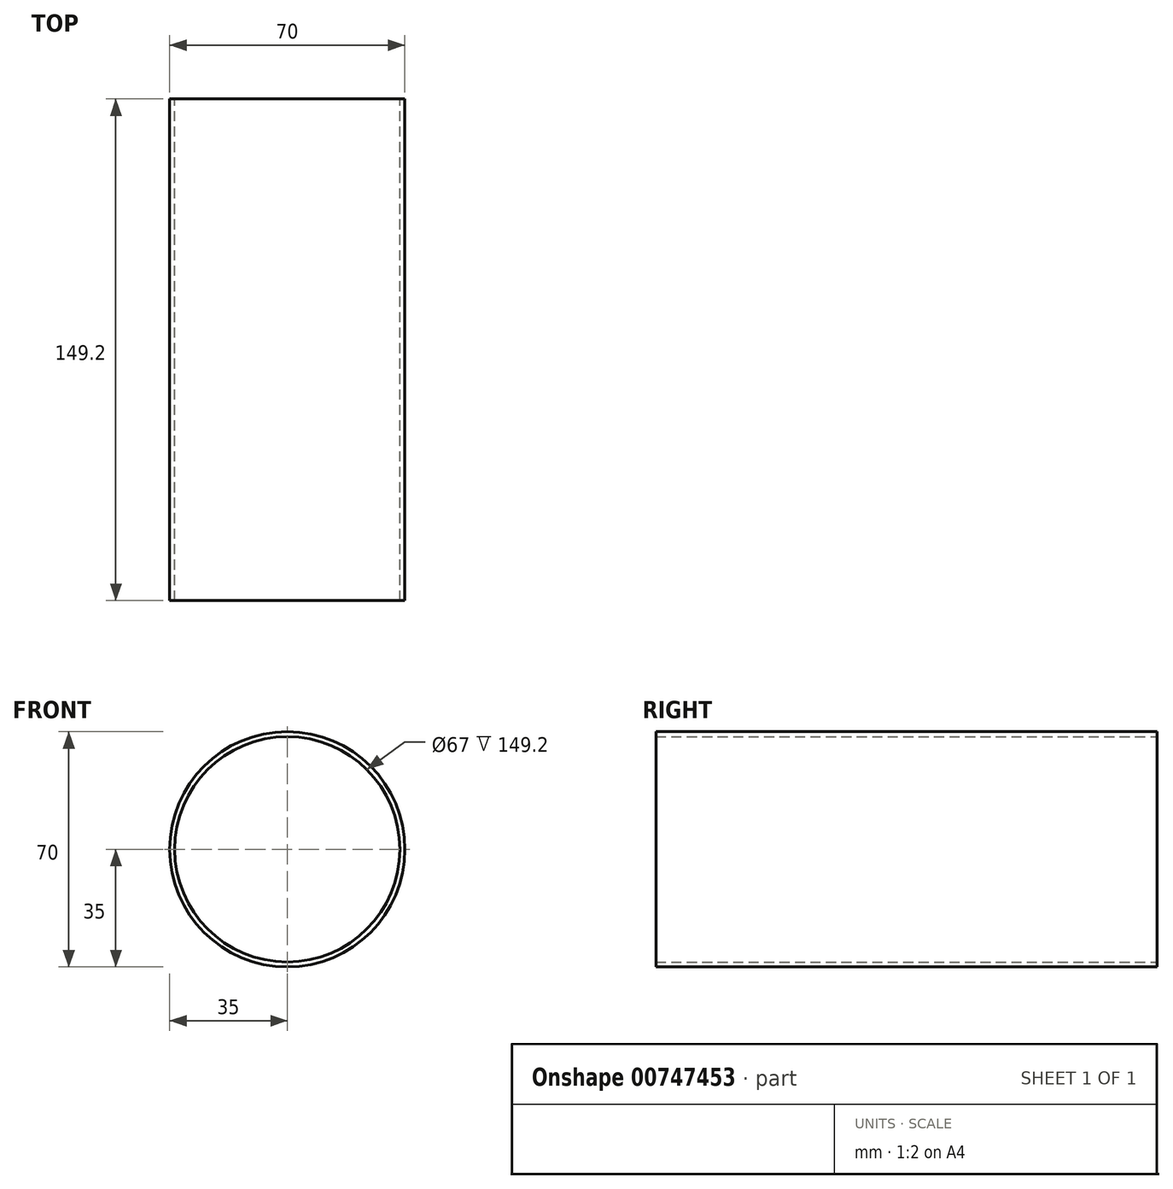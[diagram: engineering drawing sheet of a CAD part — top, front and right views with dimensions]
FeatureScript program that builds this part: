
annotation { "Feature Type Name" : "Feature", "Feature Type Description" : "" }
export const myFeature = defineFeature(function(context is Context, id is Id, definition is map)
    precondition{}
    {
        {
            var Q0;
            Q0=qCreatedBy(makeId("Front.planeOp"),FACE);
            var sketch = newSketch(context, id + "F0", { "sketchPlane" : qUnion([Q0])});
            skCircle(sketch, "E0", {"center": v(0, 0) * mm, "radius": 35 * mm});
            skCircle(sketch, "E1", {"center": v(0, 0) * mm, "radius": 33.5 * mm});
            skSolve(sketch);
        }
        {
            var Q0;
            Q0=makeQuery(id+"F0.imprint","IMPRINT",FACE,{"disambiguationData":[TD([[makeQuery(id+"F0.imprint","IMPRINT",EDGE,{"derivedFrom":sQuery(id+"F0.wireOp",EDGE,"E0")}),1.0]])]});
            extrude(context, id + "F1", {"entities" : qUnion([Q0]), "endBound" : BoundingType.SYMMETRIC, "depth" : 149.2 * mm, "offsetDistance" : 25 * mm});
        }
    });
